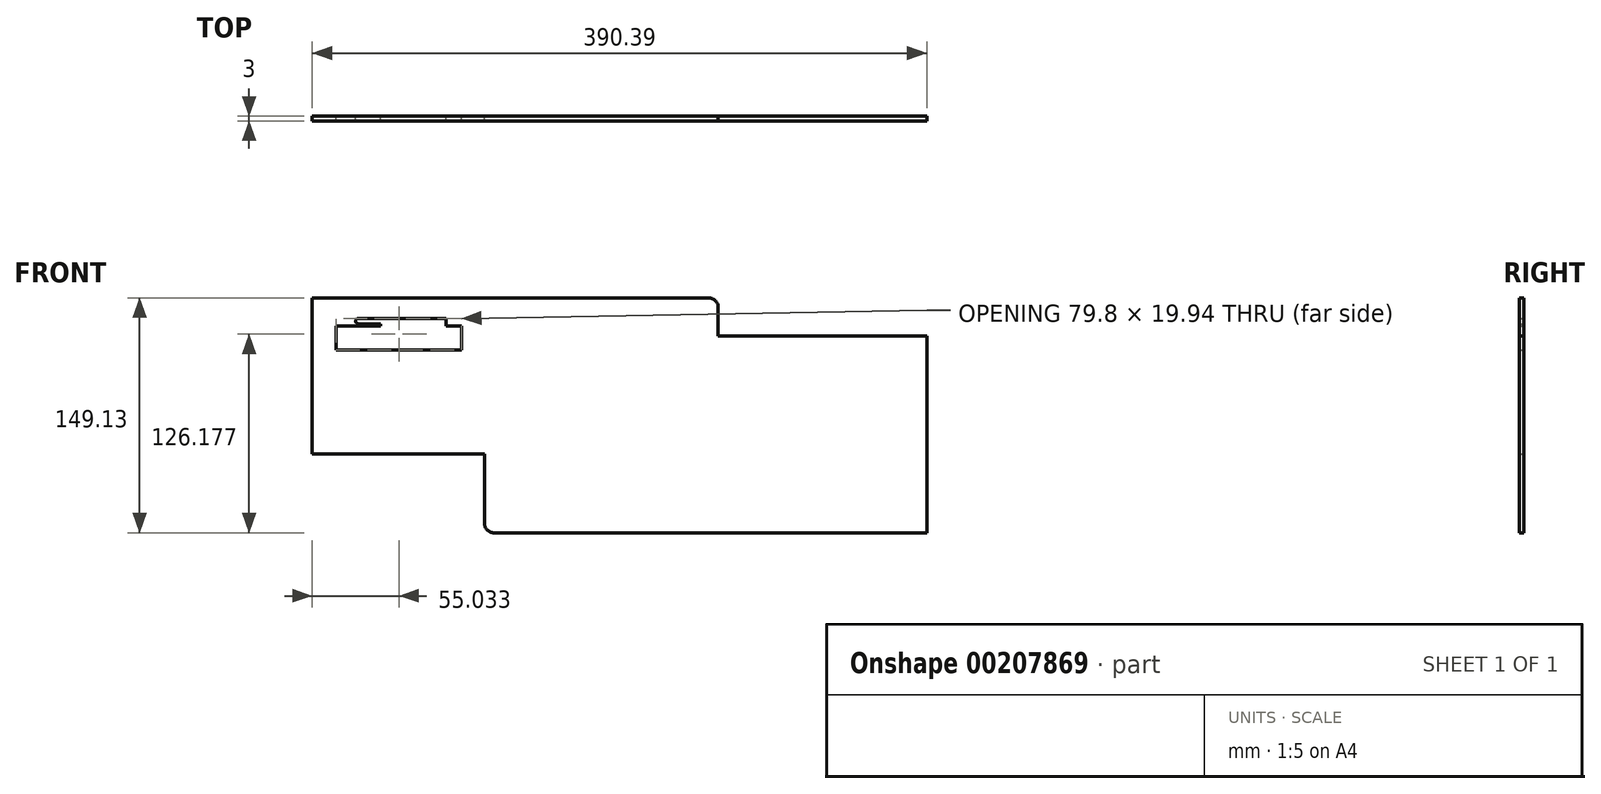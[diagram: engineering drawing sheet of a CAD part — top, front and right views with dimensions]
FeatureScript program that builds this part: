
annotation { "Feature Type Name" : "Feature", "Feature Type Description" : "" }
export const myFeature = defineFeature(function(context is Context, id is Id, definition is map)
    precondition{}
    {
        {
            var Q0;
            Q0=qCreatedBy(makeId("Front.planeOp"),FACE);
            var sketch = newSketch(context, id + "F0", { "sketchPlane" : qUnion([Q0])});
            skLineSegment(sketch, "E0", {"start": v(0, 0) * mm, "end": v(0, 99.06) * mm});
            skLineSegment(sketch, "E1", {"start": v(0, 99.06) * mm, "end": v(251.87, 99.06) * mm});
            skLineSegment(sketch, "E2", {"start": v(257.87, 93.06) * mm, "end": v(257.87, 75.06) * mm});
            skLineSegment(sketch, "E3", {"start": v(257.87, 75.06) * mm, "end": v(390.39, 75.06) * mm});
            skLineSegment(sketch, "E4", {"start": v(390.39, 75.06) * mm, "end": v(390.39, -50.07) * mm});
            skLineSegment(sketch, "E5", {"start": v(390.39, -50.07) * mm, "end": v(115.44, -50.07) * mm});
            skLineSegment(sketch, "E6", {"start": v(109.44, -44.07) * mm, "end": v(109.44, 0) * mm});
            skLineSegment(sketch, "E7", {"start": v(109.44, 0) * mm, "end": v(0, 0) * mm});
            skPoint(sketch, "E8.visualSharp", {"position": v(109.44, -50.07) * mm});
            skArc(sketch, "E8.filletArc", {"start": v(109.44, -44.07) * mm, "mid": v(111.2, -48.31) * mm, "end": v(115.44, -50.07) * mm});
            skPoint(sketch, "E9.visualSharp", {"position": v(257.87, 99.06) * mm});
            skArc(sketch, "E9.filletArc", {"start": v(257.87, 93.06) * mm, "mid": v(256.11, 97.3) * mm, "end": v(251.87, 99.06) * mm});
            skLineSegment(sketch, "E10", {"start": v(15.13, 81.12) * mm, "end": v(15.13, 66.14) * mm});
            skLineSegment(sketch, "E11", {"start": v(15.13, 81.12) * mm, "end": v(43.45, 81.12) * mm});
            skLineSegment(sketch, "E12", {"start": v(15.13, 66.14) * mm, "end": v(94.94, 66.14) * mm});
            skLineSegment(sketch, "E13", {"start": v(94.94, 66.14) * mm, "end": v(94.94, 81.12) * mm});
            skLineSegment(sketch, "E14", {"start": v(94.94, 81.12) * mm, "end": v(85.02, 81.12) * mm});
            skLineSegment(sketch, "E15", {"start": v(85.02, 81.12) * mm, "end": v(85.02, 86.08) * mm});
            skLineSegment(sketch, "E16", {"start": v(85.02, 86.08) * mm, "end": v(29.29, 86.08) * mm});
            skArc(sketch, "E17", {"start": v(29.29, 86.08) * mm, "mid": v(27.6, 84.39) * mm, "end": v(29.29, 82.7) * mm});
            skPoint(sketch, "E18", {"position": v(29.29, 81.12) * mm});
            skLineSegment(sketch, "E19", {"start": v(43.45, 81.12) * mm, "end": v(43.45, 82.7) * mm});
            skLineSegment(sketch, "E20", {"start": v(43.45, 82.7) * mm, "end": v(29.29, 82.7) * mm});
            skSolve(sketch);
        }
        {
            var Q0;
            Q0 = qSketchRegion(id + "F0", true);
            extrude(context, id + "F1", {"entities" : qUnion([Q0]), "domain" : OperationDomain.MODEL, "flatOperationType" : FlatOperationType.REMOVE, "depth" : 3 * mm, "offsetDistance" : 25.4 * mm});
        }
    });
